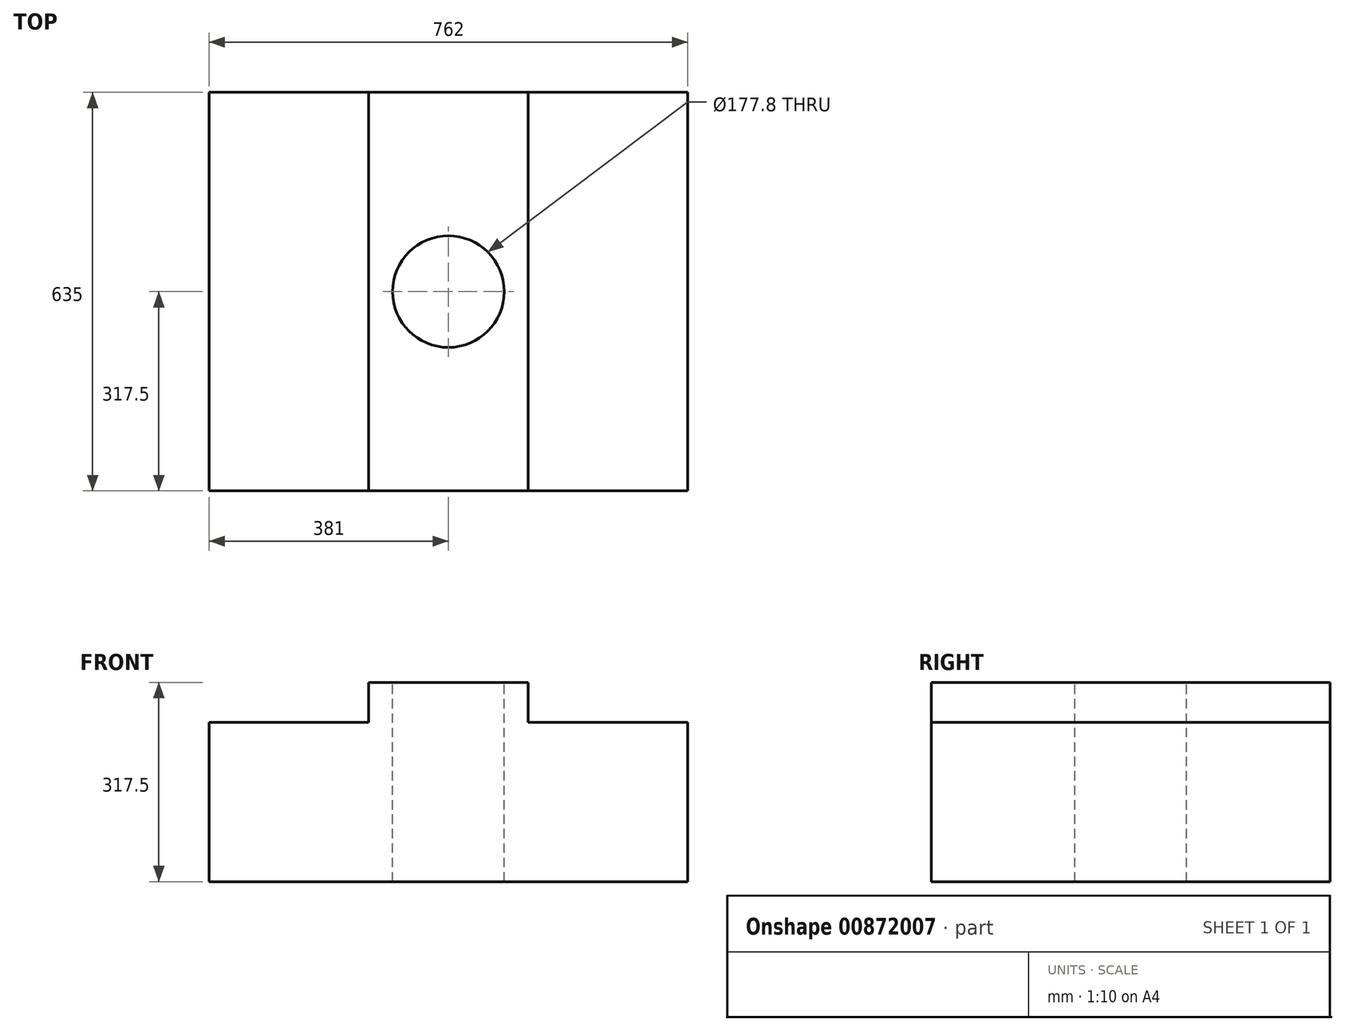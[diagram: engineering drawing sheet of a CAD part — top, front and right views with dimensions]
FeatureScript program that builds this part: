
annotation { "Feature Type Name" : "Feature", "Feature Type Description" : "" }
export const myFeature = defineFeature(function(context is Context, id is Id, definition is map)
    precondition{}
    {
        {
            var Q0;
            Q0=qCreatedBy(makeId("Front.planeOp"),FACE);
            var sketch = newSketch(context, id + "F0", { "sketchPlane" : qUnion([Q0])});
            skLineSegment(sketch, "E0", {"start": v(0, 0) * mm, "end": v(762, 0) * mm});
            skLineSegment(sketch, "E1", {"start": v(762, 0) * mm, "end": v(762, 254) * mm});
            skLineSegment(sketch, "E2", {"start": v(762, 254) * mm, "end": v(508, 254) * mm});
            skLineSegment(sketch, "E3", {"start": v(508, 254) * mm, "end": v(508, 317.5) * mm});
            skLineSegment(sketch, "E4", {"start": v(508, 317.5) * mm, "end": v(254, 317.5) * mm});
            skLineSegment(sketch, "E5", {"start": v(254, 317.5) * mm, "end": v(254, 254) * mm});
            skLineSegment(sketch, "E6", {"start": v(254, 254) * mm, "end": v(0, 254) * mm});
            skLineSegment(sketch, "E7", {"start": v(0, 254) * mm, "end": v(0, 0) * mm});
            skSolve(sketch);
        }
        {
            var Q0;
            Q0=makeQuery(id+"F0.imprint","IMPRINT",FACE,{"disambiguationData":[TD([[makeQuery(id+"F0.imprint","IMPRINT",EDGE,{"derivedFrom":sQuery(id+"F0.wireOp",EDGE,"E0")}),1.0]])]});
            extrude(context, id + "F1", {"entities" : qUnion([Q0]), "oppositeDirection" : true, "depth" : 635 * mm, "offsetDistance" : 25.4 * mm});
        }
        {
            var Q0;
            Q0=makeQuery(id+"F1.opExtrude","SWEPT_FACE",FACE,{"disambiguationData":[OSD([sQuery(id+"F0.wireOp",EDGE,"E4")])]});
            var sketch = newSketch(context, id + "F2", { "sketchPlane" : qUnion([Q0])});
            skPoint(sketch, "E8", {"position": v(381, 317.5) * mm});
            skCircle(sketch, "E9", {"center": v(381, 317.5) * mm, "radius": 88.9 * mm});
            skPoint(sketch, "E10.orphan", {"position": v(381, 0) * mm});
            skPoint(sketch, "E11.orphan", {"position": v(381, 635) * mm});
            skPoint(sketch, "E12.trimOffspring.end.orphan", {"position": v(508, 317.5) * mm});
            skPoint(sketch, "E13.start.orphan", {"position": v(254, 317.5) * mm});
            skSolve(sketch);
        }
        {
            var Q0;
            Q0=sQuery(id+"F2.wireOp",VERTEX,"E8");
            var Q1;
            Q1=makeQuery(id+"F1.opExtrude","SWEPT_BODY",BODY,{"disambiguationData":[OSD([sQuery(id+"F0.wireOp",EDGE,"E0"),sQuery(id+"F0.wireOp",EDGE,"E1"),sQuery(id+"F0.wireOp",EDGE,"E2"),sQuery(id+"F0.wireOp",EDGE,"E3"),sQuery(id+"F0.wireOp",EDGE,"E4"),sQuery(id+"F0.wireOp",EDGE,"E5"),sQuery(id+"F0.wireOp",EDGE,"E6"),sQuery(id+"F0.wireOp",EDGE,"E7")])]});
            hole(context, id + "F3", {"style" : HoleStyle.SIMPLE, "endStyle" : HoleEndStyle.THROUGH, "holeDiameter" : 177.8 * mm, "majorDiameter" : 6.35 * mm, "isTappedThrough" : true, "tappedDepth" : 12.7 * mm, "tapClearance" : 3, "locations" : qUnion([Q0]), "scope" : qUnion([Q1])});
        }
    });
